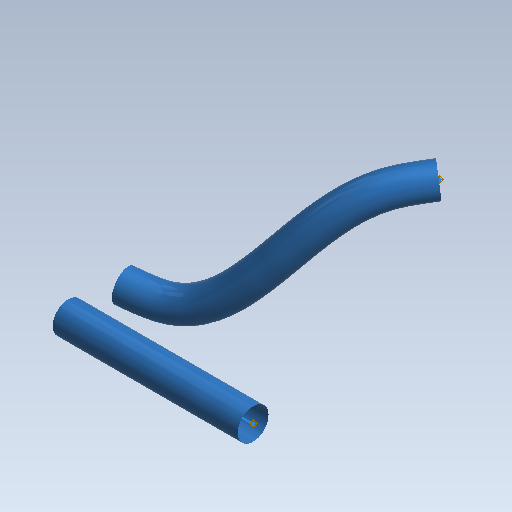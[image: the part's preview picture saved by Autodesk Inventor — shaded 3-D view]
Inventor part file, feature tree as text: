
AUTODESK INVENTOR PART (.ipt)
format: ipt  version: 2022 (Build 260153000, 153)  size: 198,144 bytes
history: native  units: mm (DEFAULTED — no unit token found)
features: other x10, plane x2, sketch x2, sweep x2
ambient origin geometry x8: Origin, YZ Plane, XZ Plane, XY Plane, X Axis, Y Axis, Z Axis, Center Point
bodies: Body1 (feature_tree), Body2 (feature_tree)
feature tree (16):
  other  "Work Point1"
  other  "Work Point2"
  other  "Wire1"
  plane  "Work Plane1"
  other  "Work Point3"
  other  "Work Point4"
  other  "Work Point7"
  other  "Work Point8"
  other  "Wire2"
  plane  "Work Plane3"
  sketch  "Sketch1"  dims[d0=0.0mm d1=0.0mm d4=0.0mm d5=0.0mm]
  other  "Srf1"
  sketch  "Sketch3"
  other  "Srf3"
  sweep  "SweepSrf1"
  sweep  "SweepSrf3"
